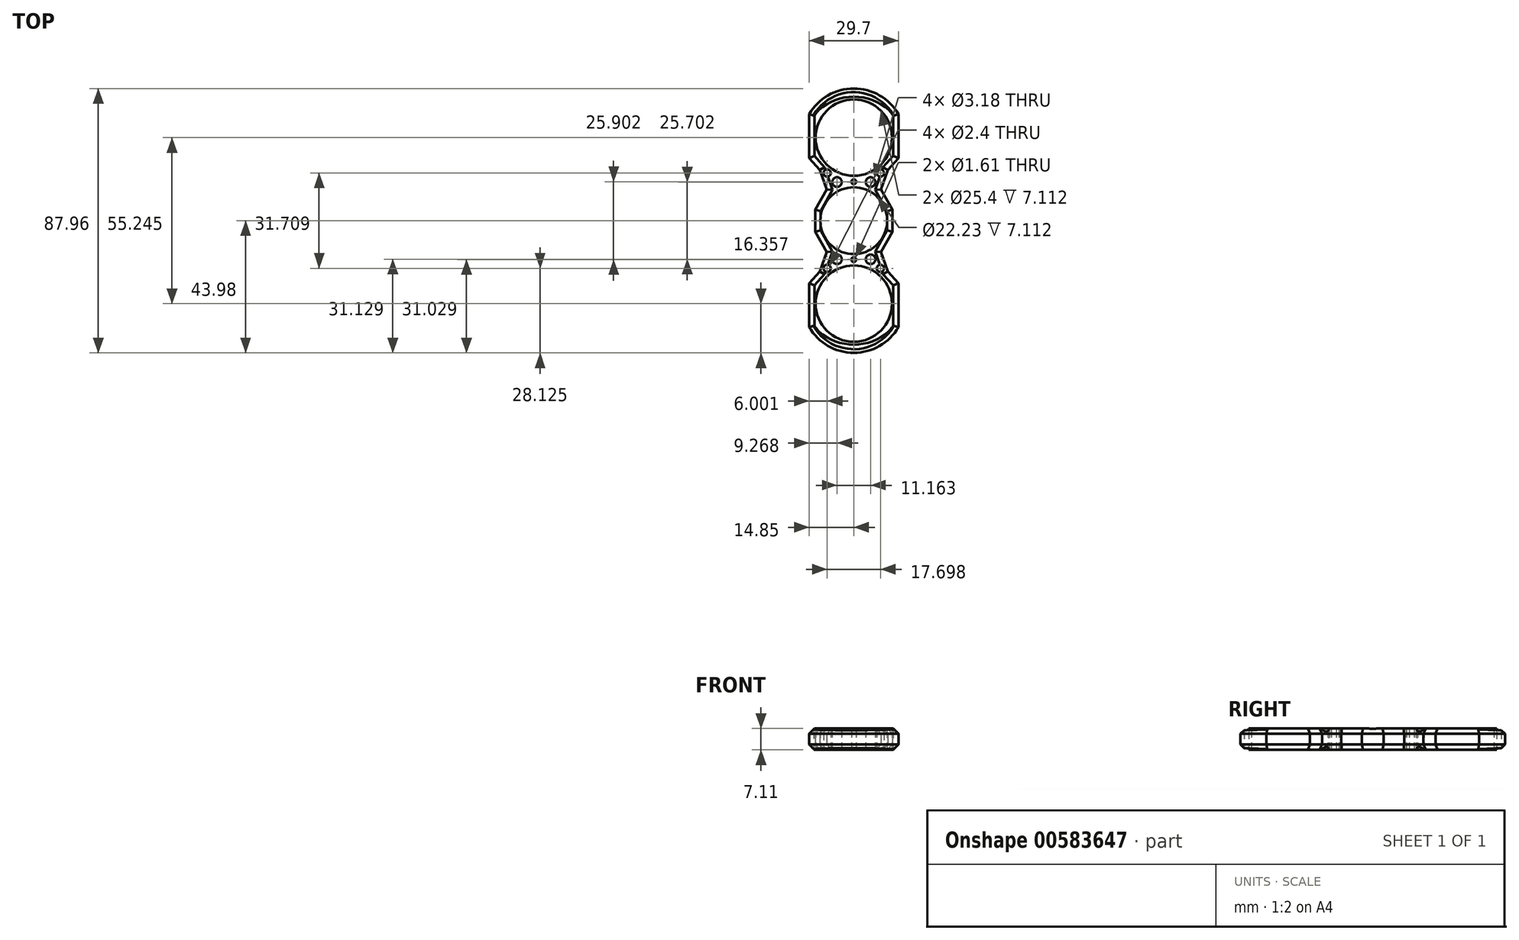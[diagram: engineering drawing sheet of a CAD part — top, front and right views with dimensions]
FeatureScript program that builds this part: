
annotation { "Feature Type Name" : "Feature", "Feature Type Description" : "" }
export const myFeature = defineFeature(function(context is Context, id is Id, definition is map)
    precondition{}
    {
        {
            var Q0;
            Q0=qCreatedBy(makeId("Top.planeOp"),FACE);
            var sketch = newSketch(context, id + "F0", { "sketchPlane" : qUnion([Q0])});
            skCircle(sketch, "E0", {"center": v(0, 0) * mm, "radius": 11.11 * mm});
            skCircle(sketch, "E1", {"center": v(0, 27.62) * mm, "radius": 12.7 * mm});
            skCircle(sketch, "E2", {"center": v(0, -27.62) * mm, "radius": 12.7 * mm});
            skLineSegment(sketch, "E3", {"start": v(-6, 42.55) * mm, "end": v(-5.71, 42.55) * mm});
            skLineSegment(sketch, "E4", {"start": v(14.85, 35.41) * mm, "end": v(14.85, 20.85) * mm});
            skLineSegment(sketch, "E5", {"start": v(14.85, 20.85) * mm, "end": v(11.28, 16.85) * mm});
            skLineSegment(sketch, "E6", {"start": v(9.05, 10.44) * mm, "end": v(12.8, 3.68) * mm});
            skLineSegment(sketch, "E7", {"start": v(-56.83, 0) * mm, "end": v(65.4, 0) * mm});
            skLineSegment(sketch, "E8", {"start": v(0, 64.82) * mm, "end": v(0, -65.68) * mm});
            skLineSegment(sketch, "E9.MirrorCS", {"start": v(-6, -42.55) * mm, "end": v(-5.71, -42.55) * mm});
            skLineSegment(sketch, "E10.MirrorCS", {"start": v(14.85, -35.41) * mm, "end": v(14.85, -20.85) * mm});
            skLineSegment(sketch, "E11.MirrorCS", {"start": v(14.85, -20.85) * mm, "end": v(11.28, -16.85) * mm});
            skLineSegment(sketch, "E12.MirrorCS", {"start": v(9.05, -10.44) * mm, "end": v(12.8, -3.68) * mm});
            skLineSegment(sketch, "E13.MirrorCS", {"start": v(-14.85, 35.41) * mm, "end": v(-14.85, 20.85) * mm});
            skLineSegment(sketch, "E14.MirrorCS", {"start": v(-14.85, 20.85) * mm, "end": v(-11.28, 16.85) * mm});
            skLineSegment(sketch, "E15.MirrorCS", {"start": v(-9.05, 10.44) * mm, "end": v(-12.8, 3.68) * mm});
            skLineSegment(sketch, "E16.MirrorCS", {"start": v(-9.05, -10.44) * mm, "end": v(-12.8, -3.68) * mm});
            skLineSegment(sketch, "E17.MirrorCS", {"start": v(-14.85, -20.85) * mm, "end": v(-11.28, -16.85) * mm});
            skLineSegment(sketch, "E18.MirrorCS", {"start": v(-14.85, -35.41) * mm, "end": v(-14.85, -20.85) * mm});
            skPoint(sketch, "E19.MirrorCS.end.orphan", {"position": v(-14.85, -35.41) * mm});
            skPoint(sketch, "E19.MirrorCS.start.orphan", {"position": v(-5.71, -42.55) * mm});
            skPoint(sketch, "E20.trimOffspring.end.orphan", {"position": v(5.71, -42.55) * mm});
            skPoint(sketch, "E21.MirrorCS.end.orphan", {"position": v(14.85, -35.41) * mm});
            skArc(sketch, "E22", {"start": v(-14.85, -35.41) * mm, "mid": v(0, -43.98) * mm, "end": v(14.85, -35.41) * mm});
            skPoint(sketch, "E23.MirrorCS.end.orphan", {"position": v(-14.85, 35.41) * mm});
            skPoint(sketch, "E23.MirrorCS.start.orphan", {"position": v(-5.71, 42.55) * mm});
            skPoint(sketch, "E24.start.orphan", {"position": v(5.71, 42.55) * mm});
            skArc(sketch, "E25.MirrorCS", {"start": v(-14.85, 35.41) * mm, "mid": v(0, 43.98) * mm, "end": v(14.85, 35.41) * mm});
            skLineSegment(sketch, "E26", {"start": v(-12.8, 3.68) * mm, "end": v(-12.8, -3.68) * mm});
            skPoint(sketch, "E27.orphan", {"position": v(-14.85, 0) * mm});
            skLineSegment(sketch, "E28.MirrorCS", {"start": v(12.8, 3.68) * mm, "end": v(12.8, -3.68) * mm});
            skPoint(sketch, "E29.orphan", {"position": v(14.85, 0) * mm});
            skLineSegment(sketch, "E30", {"start": v(11.28, 16.85) * mm, "end": v(9.05, 10.44) * mm});
            skLineSegment(sketch, "E31.MirrorCS", {"start": v(-11.28, 16.85) * mm, "end": v(-9.05, 10.44) * mm});
            skPoint(sketch, "E32.orphan", {"position": v(-7.71, 12.85) * mm});
            skPoint(sketch, "E33.orphan", {"position": v(7.71, 12.85) * mm});
            skLineSegment(sketch, "E34.MirrorCS", {"start": v(-11.28, -16.85) * mm, "end": v(-9.05, -10.44) * mm});
            skLineSegment(sketch, "E35.MirrorCS", {"start": v(11.28, -16.85) * mm, "end": v(9.05, -10.44) * mm});
            skPoint(sketch, "E36.orphan", {"position": v(-7.71, -12.85) * mm});
            skPoint(sketch, "E37.orphan", {"position": v(7.71, -12.85) * mm});
            skCircle(sketch, "E38", {"center": v(-5.58, 12.85) * mm, "radius": 1.59 * mm});
            skCircle(sketch, "E39.MirrorC", {"center": v(-5.58, -12.85) * mm, "radius": 1.59 * mm});
            skCircle(sketch, "E40.MirrorC", {"center": v(5.58, 12.85) * mm, "radius": 1.59 * mm});
            skCircle(sketch, "E41.MirrorC", {"center": v(5.58, -12.85) * mm, "radius": 1.59 * mm});
            skArc(sketch, "E42", {"start": v(-13.27, -35.21) * mm, "mid": v(-0.15, -42.77) * mm, "end": v(13.09, -35.41) * mm});
            skArc(sketch, "E43", {"start": v(-13.27, -35.21) * mm, "mid": v(-0.14, -41.25) * mm, "end": v(13.09, -35.41) * mm});
            skArc(sketch, "E44.MirrorCS", {"start": v(-13.27, 35.21) * mm, "mid": v(-0.14, 41.25) * mm, "end": v(13.09, 35.41) * mm});
            skArc(sketch, "E45.MirrorCS", {"start": v(-13.27, 35.21) * mm, "mid": v(-0.15, 42.77) * mm, "end": v(13.09, 35.41) * mm});
            skCircle(sketch, "E46", {"center": v(-8.85, 15.85) * mm, "radius": 1.2 * mm});
            skCircle(sketch, "E47", {"center": v(0, 12.95) * mm, "radius": 0.8 * mm});
            skCircle(sketch, "E48.MirrorC", {"center": v(-8.85, -15.85) * mm, "radius": 1.2 * mm});
            skCircle(sketch, "E49.MirrorC", {"center": v(0, -12.95) * mm, "radius": 0.8 * mm});
            skCircle(sketch, "E50.MirrorC", {"center": v(8.85, 15.85) * mm, "radius": 1.2 * mm});
            skCircle(sketch, "E51.MirrorC", {"center": v(8.85, -15.85) * mm, "radius": 1.2 * mm});
            skSolve(sketch);
        }
        {
            var Q0;
            {var subQ11=sQuery(id+"F0.wireOp",EDGE,"E13.MirrorCS");Q0=makeQuery(id+"F0.imprint","IMPRINT",FACE,{"disambiguationData":[TD([[makeQuery(id+"F0.imprint","IMPRINT",EDGE,{"derivedFrom":subQ11}),1.0]])]});}
            var Q1;
            {var subQ1=sQuery(id+"F0.wireOp",EDGE,"E4");Q1=makeQuery(id+"F0.imprint","IMPRINT",FACE,{"disambiguationData":[TD([[makeQuery(id+"F0.imprint","IMPRINT",EDGE,{"derivedFrom":subQ1}),-1.0]])]});}
            var Q2;
            {var subQ1=sQuery(id+"F0.wireOp",EDGE,"E16.MirrorCS");Q2=makeQuery(id+"F0.imprint","IMPRINT",FACE,{"disambiguationData":[TD([[makeQuery(id+"F0.imprint","IMPRINT",EDGE,{"derivedFrom":subQ1}),-1.0]])]});}
            var Q3;
            {var subQ4=sQuery(id+"F0.wireOp",EDGE,"E10.MirrorCS");Q3=makeQuery(id+"F0.imprint","IMPRINT",FACE,{"disambiguationData":[TD([[makeQuery(id+"F0.imprint","IMPRINT",EDGE,{"derivedFrom":subQ4}),1.0]])]});}
            extrude(context, id + "F1", {"entities" : qUnion([Q0, Q1, Q2, Q3]), "depth" : 7.11 * mm, "offsetDistance" : 25.4 * mm});
        }
        {
            var Q0;
            Q0=makeQuery(id+"F1.opExtrude","CAP_EDGE",EDGE,{"disambiguationData":[OSD([sQuery(id+"F0.wireOp",EDGE,"E25.MirrorCS")])],"isStart":false});
            var Q1;
            Q1=makeQuery(id+"F1.opExtrude","CAP_EDGE",EDGE,{"disambiguationData":[OSD([sQuery(id+"F0.wireOp",EDGE,"E13.MirrorCS")])],"isStart":false});
            var Q2;
            Q2=makeQuery(id+"F1.opExtrude","CAP_EDGE",EDGE,{"disambiguationData":[OSD([sQuery(id+"F0.wireOp",EDGE,"E4")])],"isStart":false});
            var Q3;
            Q3=makeQuery(id+"F1.opExtrude","CAP_EDGE",EDGE,{"disambiguationData":[OSD([sQuery(id+"F0.wireOp",EDGE,"E14.MirrorCS")])],"isStart":false});
            var Q4;
            Q4=makeQuery(id+"F1.opExtrude","CAP_EDGE",EDGE,{"disambiguationData":[OSD([sQuery(id+"F0.wireOp",EDGE,"E31.MirrorCS")])],"isStart":false});
            var Q5;
            Q5=makeQuery(id+"F1.opExtrude","CAP_EDGE",EDGE,{"disambiguationData":[OSD([sQuery(id+"F0.wireOp",EDGE,"E15.MirrorCS")])],"isStart":false});
            var Q6;
            Q6=makeQuery(id+"F1.opExtrude","CAP_EDGE",EDGE,{"disambiguationData":[OSD([sQuery(id+"F0.wireOp",EDGE,"E30")])],"isStart":false});
            var Q7;
            Q7=makeQuery(id+"F1.opExtrude","CAP_EDGE",EDGE,{"disambiguationData":[OSD([sQuery(id+"F0.wireOp",EDGE,"E5")])],"isStart":false});
            var Q8;
            Q8=makeQuery(id+"F1.opExtrude","CAP_EDGE",EDGE,{"disambiguationData":[OSD([sQuery(id+"F0.wireOp",EDGE,"E6")])],"isStart":false});
            var Q9;
            Q9=makeQuery(id+"F1.opExtrude","CAP_EDGE",EDGE,{"disambiguationData":[OSD([sQuery(id+"F0.wireOp",EDGE,"E28.MirrorCS")])],"isStart":false});
            var Q10;
            Q10=makeQuery(id+"F1.opExtrude","CAP_EDGE",EDGE,{"disambiguationData":[OSD([sQuery(id+"F0.wireOp",EDGE,"E26")])],"isStart":false});
            var Q11;
            Q11=makeQuery(id+"F1.opExtrude","CAP_EDGE",EDGE,{"disambiguationData":[OSD([sQuery(id+"F0.wireOp",EDGE,"E16.MirrorCS")])],"isStart":false});
            var Q12;
            Q12=makeQuery(id+"F1.opExtrude","CAP_EDGE",EDGE,{"disambiguationData":[OSD([sQuery(id+"F0.wireOp",EDGE,"E34.MirrorCS")])],"isStart":false});
            var Q13;
            Q13=makeQuery(id+"F1.opExtrude","CAP_EDGE",EDGE,{"disambiguationData":[OSD([sQuery(id+"F0.wireOp",EDGE,"E17.MirrorCS")])],"isStart":false});
            var Q14;
            Q14=makeQuery(id+"F1.opExtrude","CAP_EDGE",EDGE,{"disambiguationData":[OSD([sQuery(id+"F0.wireOp",EDGE,"E18.MirrorCS")])],"isStart":false});
            var Q15;
            Q15=makeQuery(id+"F1.opExtrude","CAP_EDGE",EDGE,{"disambiguationData":[OSD([sQuery(id+"F0.wireOp",EDGE,"E35.MirrorCS")])],"isStart":false});
            var Q16;
            Q16=makeQuery(id+"F1.opExtrude","CAP_EDGE",EDGE,{"disambiguationData":[OSD([sQuery(id+"F0.wireOp",EDGE,"E12.MirrorCS")])],"isStart":false});
            var Q17;
            Q17=makeQuery(id+"F1.opExtrude","CAP_EDGE",EDGE,{"disambiguationData":[OSD([sQuery(id+"F0.wireOp",EDGE,"E11.MirrorCS")])],"isStart":false});
            var Q18;
            Q18=makeQuery(id+"F1.opExtrude","CAP_EDGE",EDGE,{"disambiguationData":[OSD([sQuery(id+"F0.wireOp",EDGE,"E10.MirrorCS")])],"isStart":false});
            var Q19;
            Q19=makeQuery(id+"F1.opExtrude","CAP_EDGE",EDGE,{"disambiguationData":[OSD([sQuery(id+"F0.wireOp",EDGE,"E22")])],"isStart":false});
            var Q20;
            Q20=makeQuery(id+"F1.opExtrude","CAP_EDGE",EDGE,{"disambiguationData":[OSD([sQuery(id+"F0.wireOp",EDGE,"E25.MirrorCS")])],"isStart":true});
            var Q21;
            Q21=makeQuery(id+"F1.opExtrude","CAP_EDGE",EDGE,{"disambiguationData":[OSD([sQuery(id+"F0.wireOp",EDGE,"E4")])],"isStart":true});
            var Q22;
            Q22=makeQuery(id+"F1.opExtrude","CAP_EDGE",EDGE,{"disambiguationData":[OSD([sQuery(id+"F0.wireOp",EDGE,"E13.MirrorCS")])],"isStart":true});
            var Q23;
            Q23=makeQuery(id+"F1.opExtrude","CAP_EDGE",EDGE,{"disambiguationData":[OSD([sQuery(id+"F0.wireOp",EDGE,"E14.MirrorCS")])],"isStart":true});
            var Q24;
            Q24=makeQuery(id+"F1.opExtrude","CAP_EDGE",EDGE,{"disambiguationData":[OSD([sQuery(id+"F0.wireOp",EDGE,"E31.MirrorCS")])],"isStart":true});
            var Q25;
            Q25=makeQuery(id+"F1.opExtrude","CAP_EDGE",EDGE,{"disambiguationData":[OSD([sQuery(id+"F0.wireOp",EDGE,"E15.MirrorCS")])],"isStart":true});
            var Q26;
            Q26=makeQuery(id+"F1.opExtrude","CAP_EDGE",EDGE,{"disambiguationData":[OSD([sQuery(id+"F0.wireOp",EDGE,"E26")])],"isStart":true});
            var Q27;
            Q27=makeQuery(id+"F1.opExtrude","CAP_EDGE",EDGE,{"disambiguationData":[OSD([sQuery(id+"F0.wireOp",EDGE,"E16.MirrorCS")])],"isStart":true});
            var Q28;
            Q28=makeQuery(id+"F1.opExtrude","CAP_EDGE",EDGE,{"disambiguationData":[OSD([sQuery(id+"F0.wireOp",EDGE,"E34.MirrorCS")])],"isStart":true});
            var Q29;
            Q29=makeQuery(id+"F1.opExtrude","CAP_EDGE",EDGE,{"disambiguationData":[OSD([sQuery(id+"F0.wireOp",EDGE,"E17.MirrorCS")])],"isStart":true});
            var Q30;
            Q30=makeQuery(id+"F1.opExtrude","CAP_EDGE",EDGE,{"disambiguationData":[OSD([sQuery(id+"F0.wireOp",EDGE,"E18.MirrorCS")])],"isStart":true});
            var Q31;
            Q31=makeQuery(id+"F1.opExtrude","CAP_EDGE",EDGE,{"disambiguationData":[OSD([sQuery(id+"F0.wireOp",EDGE,"E22")])],"isStart":true});
            var Q32;
            Q32=makeQuery(id+"F1.opExtrude","CAP_EDGE",EDGE,{"disambiguationData":[OSD([sQuery(id+"F0.wireOp",EDGE,"E17.MirrorCS")])],"isStart":true});
            var Q33;
            Q33=makeQuery(id+"F1.opExtrude","CAP_EDGE",EDGE,{"disambiguationData":[OSD([sQuery(id+"F0.wireOp",EDGE,"E5")])],"isStart":true});
            var Q34;
            Q34=makeQuery(id+"F1.opExtrude","CAP_EDGE",EDGE,{"disambiguationData":[OSD([sQuery(id+"F0.wireOp",EDGE,"E30")])],"isStart":true});
            var Q35;
            Q35=makeQuery(id+"F1.opExtrude","CAP_EDGE",EDGE,{"disambiguationData":[OSD([sQuery(id+"F0.wireOp",EDGE,"E6")])],"isStart":true});
            var Q36;
            Q36=makeQuery(id+"F1.opExtrude","CAP_EDGE",EDGE,{"disambiguationData":[OSD([sQuery(id+"F0.wireOp",EDGE,"E28.MirrorCS")])],"isStart":true});
            var Q37;
            Q37=makeQuery(id+"F1.opExtrude","CAP_EDGE",EDGE,{"disambiguationData":[OSD([sQuery(id+"F0.wireOp",EDGE,"E12.MirrorCS")])],"isStart":true});
            var Q38;
            Q38=makeQuery(id+"F1.opExtrude","CAP_EDGE",EDGE,{"disambiguationData":[OSD([sQuery(id+"F0.wireOp",EDGE,"E35.MirrorCS")])],"isStart":true});
            var Q39;
            Q39=makeQuery(id+"F1.opExtrude","CAP_EDGE",EDGE,{"disambiguationData":[OSD([sQuery(id+"F0.wireOp",EDGE,"E11.MirrorCS")])],"isStart":true});
            var Q40;
            Q40=makeQuery(id+"F1.opExtrude","CAP_EDGE",EDGE,{"disambiguationData":[OSD([sQuery(id+"F0.wireOp",EDGE,"E10.MirrorCS")])],"isStart":true});
            var Q41;
            Q41=makeQuery(id+"F1.opExtrude","CAP_EDGE",EDGE,{"disambiguationData":[OSD([sQuery(id+"F0.wireOp",EDGE,"E35.MirrorCS")])],"isStart":true});
            chamfer(context, id + "F2", {"entities" : qUnion([Q0, Q1, Q2, Q3, Q4, Q5, Q6, Q7, Q8, Q9, Q10, Q11, Q12, Q13, Q14, Q15, Q16, Q17, Q18, Q19, Q20, Q21, Q22, Q23, Q24, Q25, Q26, Q27, Q28, Q29, Q30, Q31, Q32, Q33, Q34, Q35, Q36, Q37, Q38, Q39, Q40, Q41]), "width" : 1.78 * mm, "tangentPropagation" : true});
        }
    });
